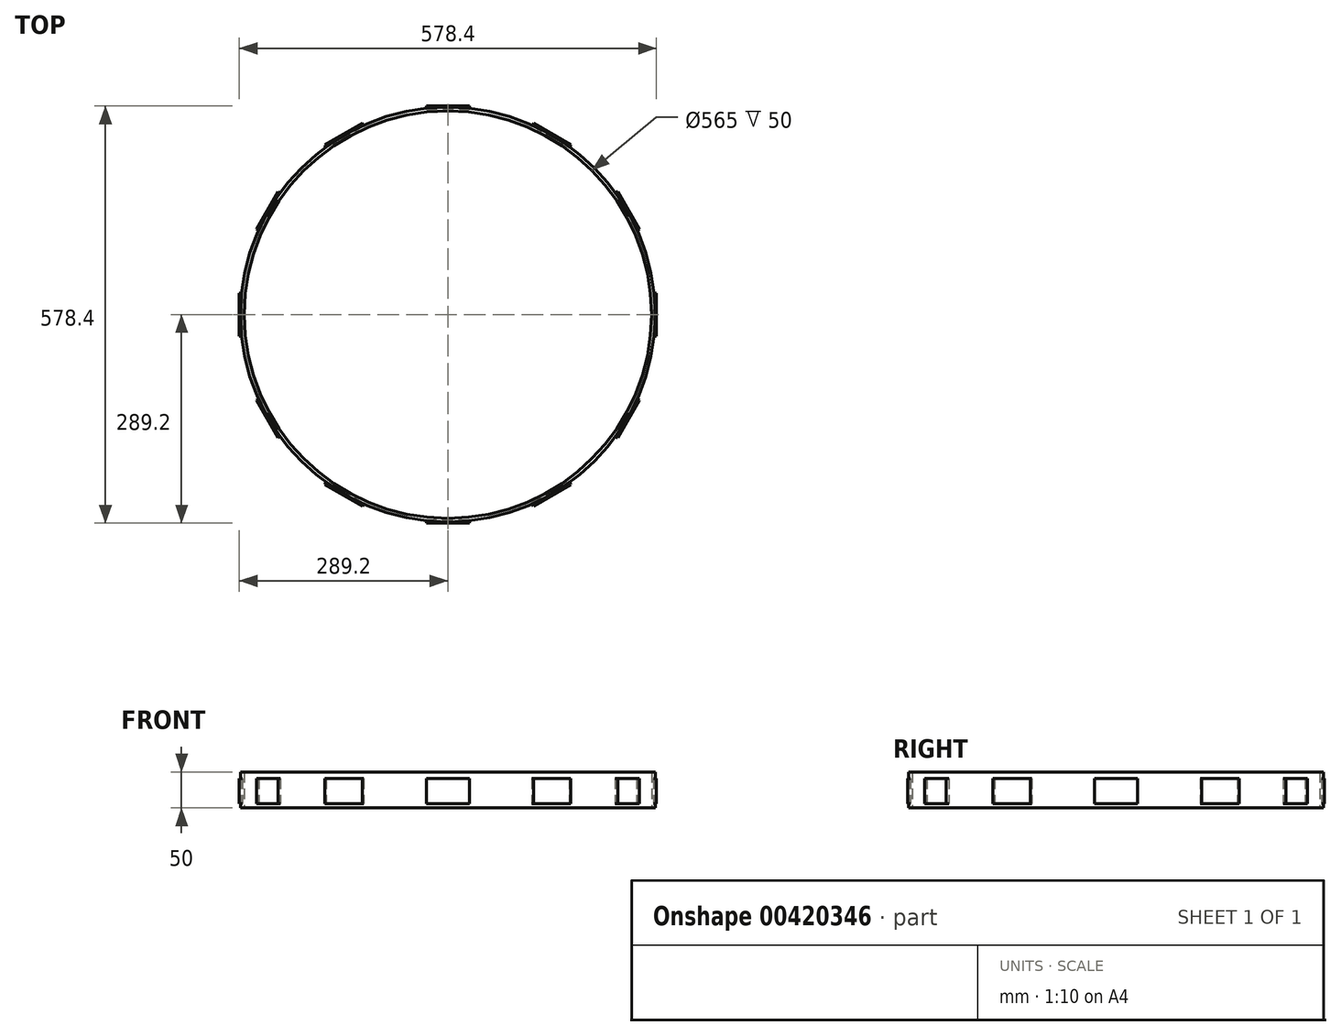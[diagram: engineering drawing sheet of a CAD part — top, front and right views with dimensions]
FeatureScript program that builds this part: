
annotation { "Feature Type Name" : "Feature", "Feature Type Description" : "" }
export const myFeature = defineFeature(function(context is Context, id is Id, definition is map)
    precondition{}
    {
        {
            var Q0;
            Q0=qCreatedBy(makeId("Top.planeOp"),FACE);
            var sketch = newSketch(context, id + "F0", { "sketchPlane" : qUnion([Q0])});
            skCircle(sketch, "E0", {"center": v(0, 0) * mm, "radius": 282.5 * mm});
            skCircle(sketch, "E1.0", {"center": v(0, 0) * mm, "radius": 287.5 * mm});
            skSolve(sketch);
        }
        {
            var Q0;
            Q0 = qSketchRegion(id + "F0", true);
            extrude(context, id + "F1", {"entities" : qUnion([Q0]), "depth" : 50 * mm});
        }
        {
            var Q0;
            Q0=qCreatedBy(makeId("Front.planeOp"),FACE);
            var sketch = newSketch(context, id + "F2", { "sketchPlane" : qUnion([Q0])});
            skLineSegment(sketch, "E2.0", {"start": v(-287.5, 50) * mm, "end": v(0, 50) * mm, "construction": true});
            skPoint(sketch, "E3.orphan", {"position": v(287.5, 50) * mm});
            skLineSegment(sketch, "E4", {"start": v(0, 0) * mm, "end": v(0, 288) * mm});
            skArc(sketch, "E5", {"start": v(0, 288) * mm, "mid": v(-194.5, 230.3) * mm, "end": v(-287.5, 50) * mm});
            skSolve(sketch);
        }
        {
            var Q0;
            Q0=sQuery(id+"F2.wireOp",EDGE,"E5");
            var Q1;
            Q1=sQuery(id+"F2.wireOp",EDGE,"E4");
            revolve(context, id + "F3", {"bodyType" : ToolBodyType.SURFACE, "surfaceEntities" : qUnion([Q0]), "axis" : qUnion([Q1]), "revolveType" : RevolveType.FULL});
        }
        {
            var Q0;
            Q0=qCreatedBy(makeId("Front.planeOp"),FACE);
            cPlane(context, id + "F4", {"entities" : qUnion([Q0]), "cplaneType" : CPlaneType.OFFSET, "offset" : 287.2 * mm, "width" : 150 * mm, "height" : 150 * mm});
        }
        {
            var Q0;
            Q0=qCreatedBy(id+"F4.planeOp",FACE);
            var sketch = newSketch(context, id + "F5", { "sketchPlane" : qUnion([Q0])});
            skLineSegment(sketch, "E6.bottom", {"start": v(30, 41) * mm, "end": v(-30, 41) * mm});
            skLineSegment(sketch, "E6.top", {"start": v(30, 6) * mm, "end": v(-30, 6) * mm});
            skLineSegment(sketch, "E6.left", {"start": v(30, 41) * mm, "end": v(30, 6) * mm});
            skLineSegment(sketch, "E6.right", {"start": v(-30, 41) * mm, "end": v(-30, 6) * mm});
            skLineSegment(sketch, "E7", {"start": v(0, -18.28) * mm, "end": v(0, 63.42) * mm, "construction": true});
            skSolve(sketch);
        }
        {
            var Q0;
            Q0 = qSketchRegion(id + "F5", true);
            extrude(context, id + "F6", {"entities" : qUnion([Q0]), "endBound" : BoundingType.SYMMETRIC, "depth" : 4 * mm});
        }
        {
            var Q0;
            Q0=makeQuery(id+"F6.opExtrude","SWEPT_BODY",BODY,{"disambiguationData":[OSD([sQuery(id+"F5.wireOp",EDGE,"E6.bottom"),sQuery(id+"F5.wireOp",EDGE,"E6.top"),sQuery(id+"F5.wireOp",EDGE,"E6.left"),sQuery(id+"F5.wireOp",EDGE,"E6.right")])]});
            var Q1;
            Q1=makeQuery(id+"F1.opExtrude","SWEPT_FACE",FACE,{"disambiguationData":[OSD([sQuery(id+"F0.wireOp",EDGE,"E1.0")])]});
            circularPattern(context, id + "F7", {"entities" : qUnion([Q0]), "axis" : qUnion([Q1]), "angle" : 360 * degree, "instanceCount" : 12, "equalSpace" : true});
        }
    });
